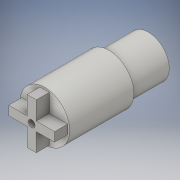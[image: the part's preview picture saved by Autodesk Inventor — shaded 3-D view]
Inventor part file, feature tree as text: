
AUTODESK INVENTOR PART (.ipt)
format: ipt  version: 2016 (Build 200138000, 138)  size: 139,776 bytes
history: native  units: in
note: dims shown in document units (in); Inventor stores cm internally (conversion verified against a paired STEP export)
features: extrude x4, sketch x4
ambient origin geometry x8: Origin, YZ Plane, XZ Plane, XY Plane, X Axis, Y Axis, Z Axis, Center Point
bodies: Solid1 (feature_tree)
feature tree (8):
  extrude  "Extrusion1"  Depth=0.9646in TaperAngle=0.0deg
  extrude  "Extrusion2"  Depth=0.5906in TaperAngle=0.0deg
  extrude  "Extrusion3"  Depth=0.1969in
  extrude  "Extrusion4"  Depth=0.2756in
  sketch  "Sketch1"  dims[d0=0.748in d1=0.9646in d2=0.0in]
  sketch  "Sketch2"  dims[d3=0.6299in d4=0.5906in d5=0.0in]
  sketch  "Sketch3"  dims[d21=0.1969in d22=0.0in d23=0.1024in]
  sketch  "Sketch4"  dims[d24=1.6905in d25=0.0in d26=0.3445in d27=0.0689in d28=0.2756in d29=0.2756in d30=0.1378in d31=0.2756in d33=0.2756in d34=0.1378in d35=0.2756in d36=0.2756in d37=0.1378in d38=0.2756in d39=0.2756in]
